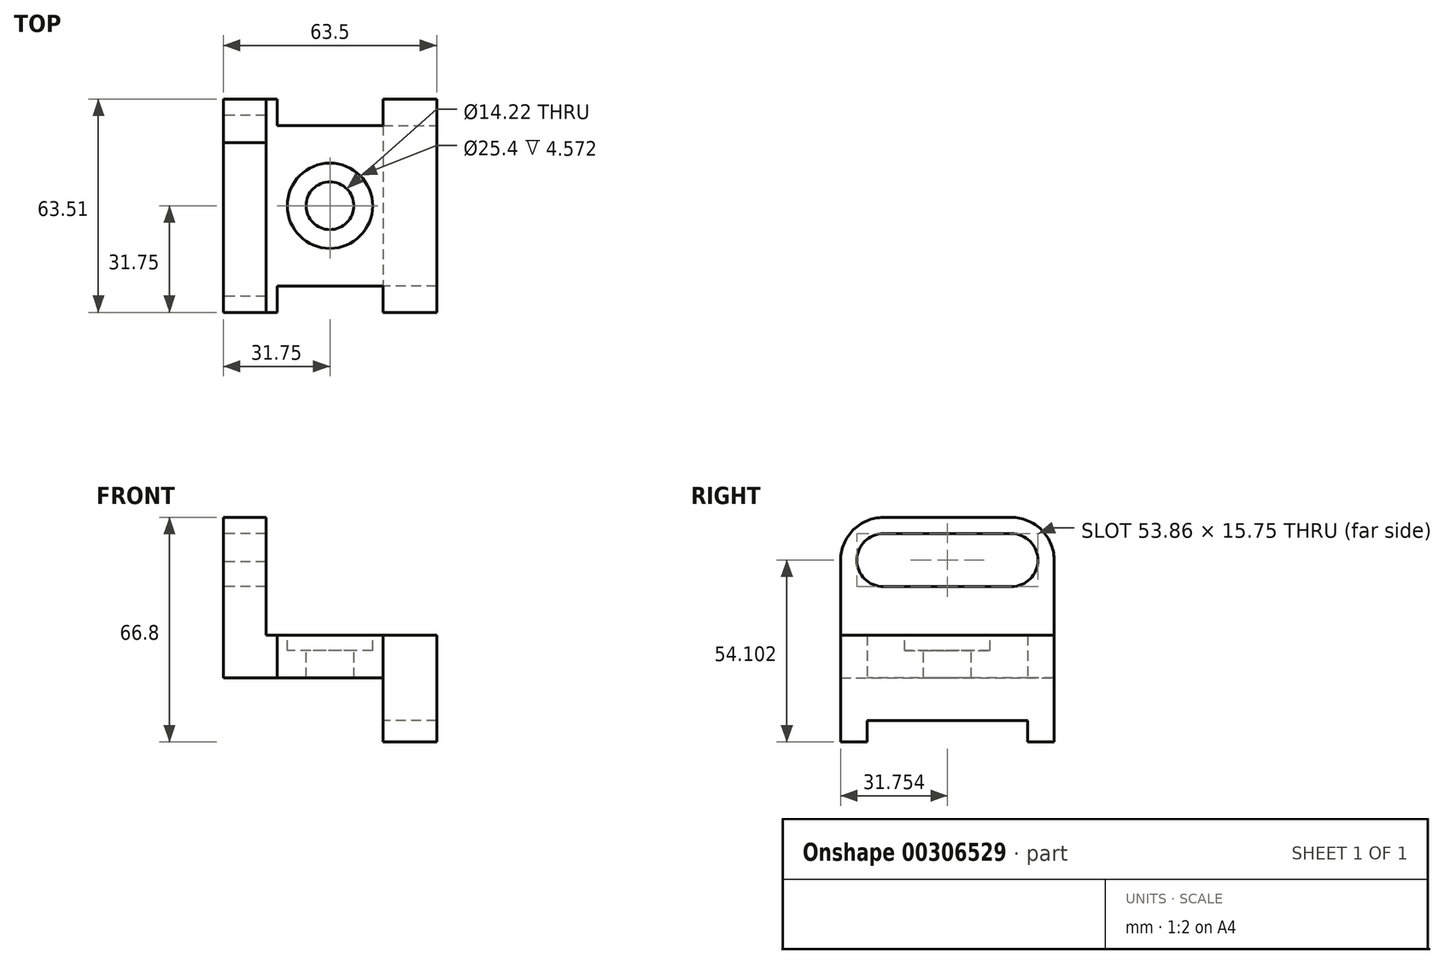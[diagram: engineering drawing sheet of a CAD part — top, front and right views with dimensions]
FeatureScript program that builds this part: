
annotation { "Feature Type Name" : "Feature", "Feature Type Description" : "" }
export const myFeature = defineFeature(function(context is Context, id is Id, definition is map)
    precondition{}
    {
        {
            var Q0;
            Q0=qCreatedBy(makeId("Top.planeOp"),FACE);
            var sketch = newSketch(context, id + "F0", { "sketchPlane" : qUnion([Q0])});
            skLineSegment(sketch, "E0.bottom", {"start": v(0, 0) * mm, "end": v(16, 0) * mm});
            skLineSegment(sketch, "E0.top", {"start": v(0, 63.5) * mm, "end": v(16, 63.5) * mm});
            skLineSegment(sketch, "E0.left", {"start": v(0, 0) * mm, "end": v(0, 63.5) * mm});
            skLineSegment(sketch, "E0.right", {"start": v(63.5, 0) * mm, "end": v(63.5, 63.5) * mm});
            skPoint(sketch, "E1", {"position": v(16, 63.5) * mm});
            skPoint(sketch, "E2", {"position": v(47.5, 63.5) * mm});
            skLineSegment(sketch, "E3.top", {"start": v(16, 55.63) * mm, "end": v(47.5, 55.63) * mm});
            skLineSegment(sketch, "E3.left", {"start": v(16, 63.5) * mm, "end": v(16, 55.63) * mm});
            skLineSegment(sketch, "E3.right", {"start": v(47.5, 63.5) * mm, "end": v(47.5, 55.63) * mm});
            skLineSegment(sketch, "E4.trimOffspring", {"start": v(47.5, 63.5) * mm, "end": v(63.5, 63.5) * mm});
            skLineSegment(sketch, "E5.MirrorCS", {"start": v(47.5, 0) * mm, "end": v(63.5, 0) * mm});
            skLineSegment(sketch, "E6.MirrorCS", {"start": v(47.5, 0) * mm, "end": v(47.5, 7.87) * mm});
            skLineSegment(sketch, "E7.MirrorCS", {"start": v(16, 7.87) * mm, "end": v(47.5, 7.87) * mm});
            skLineSegment(sketch, "E8.MirrorCS", {"start": v(16, 0) * mm, "end": v(16, 7.87) * mm});
            skPoint(sketch, "E9.end.orphan", {"position": v(63.5, 31.75) * mm});
            skPoint(sketch, "E9.start.orphan", {"position": v(0, 31.75) * mm});
            skPoint(sketch, "E10.centerSnap0", {"position": v(31.75, 55.63) * mm});
            skSolve(sketch);
        }
        {
            var Q0;
            Q0 = qSketchRegion(id + "F0", true);
            extrude(context, id + "F1", {"entities" : qUnion([Q0]), "depth" : 12.7 * mm});
        }
        {
            var Q0;
            Q0=makeQuery(id+"F1.opExtrude","CAP_FACE",FACE,{"disambiguationData":[OSD([sQuery(id+"F0.wireOp",EDGE,"E0.top"),sQuery(id+"F0.wireOp",EDGE,"E0.left"),sQuery(id+"F0.wireOp",EDGE,"E0.right"),sQuery(id+"F0.wireOp",EDGE,"E3.top"),sQuery(id+"F0.wireOp",EDGE,"E3.left"),sQuery(id+"F0.wireOp",EDGE,"E3.right"),sQuery(id+"F0.wireOp",EDGE,"E4.trimOffspring"),sQuery(id+"F0.wireOp",EDGE,"E6.MirrorCS"),sQuery(id+"F0.wireOp",EDGE,"E7.MirrorCS"),sQuery(id+"F0.wireOp",EDGE,"E0.bottom"),sQuery(id+"F0.wireOp",EDGE,"E8.MirrorCS"),sQuery(id+"F0.wireOp",EDGE,"E5.MirrorCS")])],"isStart":false});
            var sketch = newSketch(context, id + "F2", { "sketchPlane" : qUnion([Q0])});
            skCircle(sketch, "E11", {"center": v(31.75, 31.75) * mm, "radius": 7.11 * mm});
            skPoint(sketch, "E11.centerSnap0", {"position": v(63.5, 31.75) * mm});
            skPoint(sketch, "E11.centerSnap1", {"position": v(31.75, 55.63) * mm});
            skSolve(sketch);
        }
        {
            var Q0;
            Q0 = qSketchRegion(id + "F2", true);
            extrude(context, id + "F3", {"entities" : qUnion([Q0]), "operationType" : NewBodyOperationType.REMOVE, "endBound" : BoundingType.THROUGH_ALL, "oppositeDirection" : true, "depth" : 25.4 * mm});
        }
        {
            var Q0;
            Q0=makeQuery(id+"F1.opExtrude","CAP_FACE",FACE,{"disambiguationData":[OSD([sQuery(id+"F0.wireOp",EDGE,"E0.top"),sQuery(id+"F0.wireOp",EDGE,"E0.left"),sQuery(id+"F0.wireOp",EDGE,"E0.right"),sQuery(id+"F0.wireOp",EDGE,"E3.top"),sQuery(id+"F0.wireOp",EDGE,"E3.left"),sQuery(id+"F0.wireOp",EDGE,"E3.right"),sQuery(id+"F0.wireOp",EDGE,"E4.trimOffspring"),sQuery(id+"F0.wireOp",EDGE,"E6.MirrorCS"),sQuery(id+"F0.wireOp",EDGE,"E7.MirrorCS"),sQuery(id+"F0.wireOp",EDGE,"E0.bottom"),sQuery(id+"F0.wireOp",EDGE,"E8.MirrorCS"),sQuery(id+"F0.wireOp",EDGE,"E5.MirrorCS")])],"isStart":false});
            var sketch = newSketch(context, id + "F4", { "sketchPlane" : qUnion([Q0])});
            skCircle(sketch, "E12", {"center": v(31.75, 31.75) * mm, "radius": 12.7 * mm});
            skSolve(sketch);
        }
        {
            var Q0;
            Q0 = qSketchRegion(id + "F4", true);
            extrude(context, id + "F5", {"entities" : qUnion([Q0]), "operationType" : NewBodyOperationType.REMOVE, "oppositeDirection" : true, "depth" : 4.57 * mm});
        }
        {
            var Q0;
            Q0=makeQuery(id+"F1.opExtrude","SWEPT_FACE",FACE,{"disambiguationData":[OSD([sQuery(id+"F0.wireOp",EDGE,"E0.left")])]});
            var sketch = newSketch(context, id + "F6", { "sketchPlane" : qUnion([Q0])});
            skLineSegment(sketch, "E13.MirrorCS", {"start": v(-63.5, 35.05) * mm, "end": v(-63.5, 12.7) * mm});
            skLineSegment(sketch, "E14", {"start": v(0, 35.05) * mm, "end": v(0, 12.7) * mm});
            skArc(sketch, "E15", {"start": v(-50.58, 47.75) * mm, "mid": v(-59.87, 43.95) * mm, "end": v(-63.5, 34.6) * mm});
            skArc(sketch, "E16", {"start": v(0, 35.05) * mm, "mid": v(-3.72, 44.03) * mm, "end": v(-12.7, 47.75) * mm});
            skLineSegment(sketch, "E17", {"start": v(-50.58, 47.75) * mm, "end": v(-12.7, 47.75) * mm});
            skPoint(sketch, "E17.startSnap0", {"position": v(-51.03, 47.75) * mm});
            skArc(sketch, "E18", {"start": v(-12.7, 27.18) * mm, "mid": v(-4.83, 35.05) * mm, "end": v(-12.7, 42.93) * mm});
            skArc(sketch, "E19", {"start": v(-50.8, 42.93) * mm, "mid": v(-58.68, 35.05) * mm, "end": v(-50.8, 27.18) * mm});
            skLineSegment(sketch, "E20", {"start": v(-50.8, 42.93) * mm, "end": v(-12.7, 42.93) * mm});
            skLineSegment(sketch, "E21", {"start": v(-50.8, 27.18) * mm, "end": v(-12.7, 27.18) * mm});
            skSolve(sketch);
        }
        {
            var Q0;
            Q0=makeQuery(id+"F6.imprint","IMPRINT",FACE,{"disambiguationData":[TD([[makeQuery(id+"F6.imprint","IMPRINT",EDGE,{"derivedFrom":sQuery(id+"F6.wireOp",EDGE,"E14")}),-1.0]])]});
            extrude(context, id + "F7", {"entities" : qUnion([Q0]), "operationType" : NewBodyOperationType.ADD, "oppositeDirection" : true, "depth" : 12.7 * mm});
        }
        {
            var Q0;
            Q0=makeQuery(id+"F1.opExtrude","CAP_FACE",FACE,{"disambiguationData":[OSD([sQuery(id+"F0.wireOp",EDGE,"E0.top"),sQuery(id+"F0.wireOp",EDGE,"E0.left"),sQuery(id+"F0.wireOp",EDGE,"E0.right"),sQuery(id+"F0.wireOp",EDGE,"E3.top"),sQuery(id+"F0.wireOp",EDGE,"E3.left"),sQuery(id+"F0.wireOp",EDGE,"E3.right"),sQuery(id+"F0.wireOp",EDGE,"E4.trimOffspring"),sQuery(id+"F0.wireOp",EDGE,"E6.MirrorCS"),sQuery(id+"F0.wireOp",EDGE,"E7.MirrorCS"),sQuery(id+"F0.wireOp",EDGE,"E0.bottom"),sQuery(id+"F0.wireOp",EDGE,"E8.MirrorCS"),sQuery(id+"F0.wireOp",EDGE,"E5.MirrorCS")])],"isStart":true});
            var sketch = newSketch(context, id + "F8", { "sketchPlane" : qUnion([Q0])});
            skLineSegment(sketch, "E22.bottom", {"start": v(47.5, 0) * mm, "end": v(63.5, 0) * mm});
            skLineSegment(sketch, "E22.top", {"start": v(47.5, -7.87) * mm, "end": v(63.5, -7.87) * mm});
            skLineSegment(sketch, "E22.left", {"start": v(47.5, 0) * mm, "end": v(47.5, -7.87) * mm});
            skLineSegment(sketch, "E22.right", {"start": v(63.5, 0) * mm, "end": v(63.5, -7.87) * mm});
            skLineSegment(sketch, "E23.bottom", {"start": v(47.5, -55.63) * mm, "end": v(63.5, -55.63) * mm});
            skLineSegment(sketch, "E23.top", {"start": v(47.5, -63.5) * mm, "end": v(63.5, -63.5) * mm});
            skLineSegment(sketch, "E23.left", {"start": v(47.5, -55.63) * mm, "end": v(47.5, -63.5) * mm});
            skLineSegment(sketch, "E23.right", {"start": v(63.5, -55.63) * mm, "end": v(63.5, -63.5) * mm});
            skSolve(sketch);
        }
        {
            var Q0;
            Q0 = qSketchRegion(id + "F8", true);
            extrude(context, id + "F9", {"entities" : qUnion([Q0]), "operationType" : NewBodyOperationType.ADD, "depth" : 19.05 * mm});
        }
        {
            var Q0;
            Q0=makeQuery(id+"F9.opExtrude","SWEPT_FACE",FACE,{"disambiguationData":[OSD([sQuery(id+"F8.wireOp",EDGE,"E22.top")])]});
            var sketch = newSketch(context, id + "F10", { "sketchPlane" : qUnion([Q0])});
            skLineSegment(sketch, "E24.bottom", {"start": v(-63.5, 0) * mm, "end": v(-47.5, 0) * mm});
            skLineSegment(sketch, "E24.top", {"start": v(-63.5, -12.7) * mm, "end": v(-47.5, -12.7) * mm});
            skLineSegment(sketch, "E24.left", {"start": v(-63.5, 0) * mm, "end": v(-63.5, -12.7) * mm});
            skLineSegment(sketch, "E24.right", {"start": v(-47.5, 0) * mm, "end": v(-47.5, -12.7) * mm});
            skSolve(sketch);
        }
        {
            var Q0;
            Q0 = qSketchRegion(id + "F10", true);
            extrude(context, id + "F11", {"entities" : qUnion([Q0]), "operationType" : NewBodyOperationType.ADD, "endBound" : BoundingType.UP_TO_NEXT, "depth" : 54.36 * mm});
        }
    });
